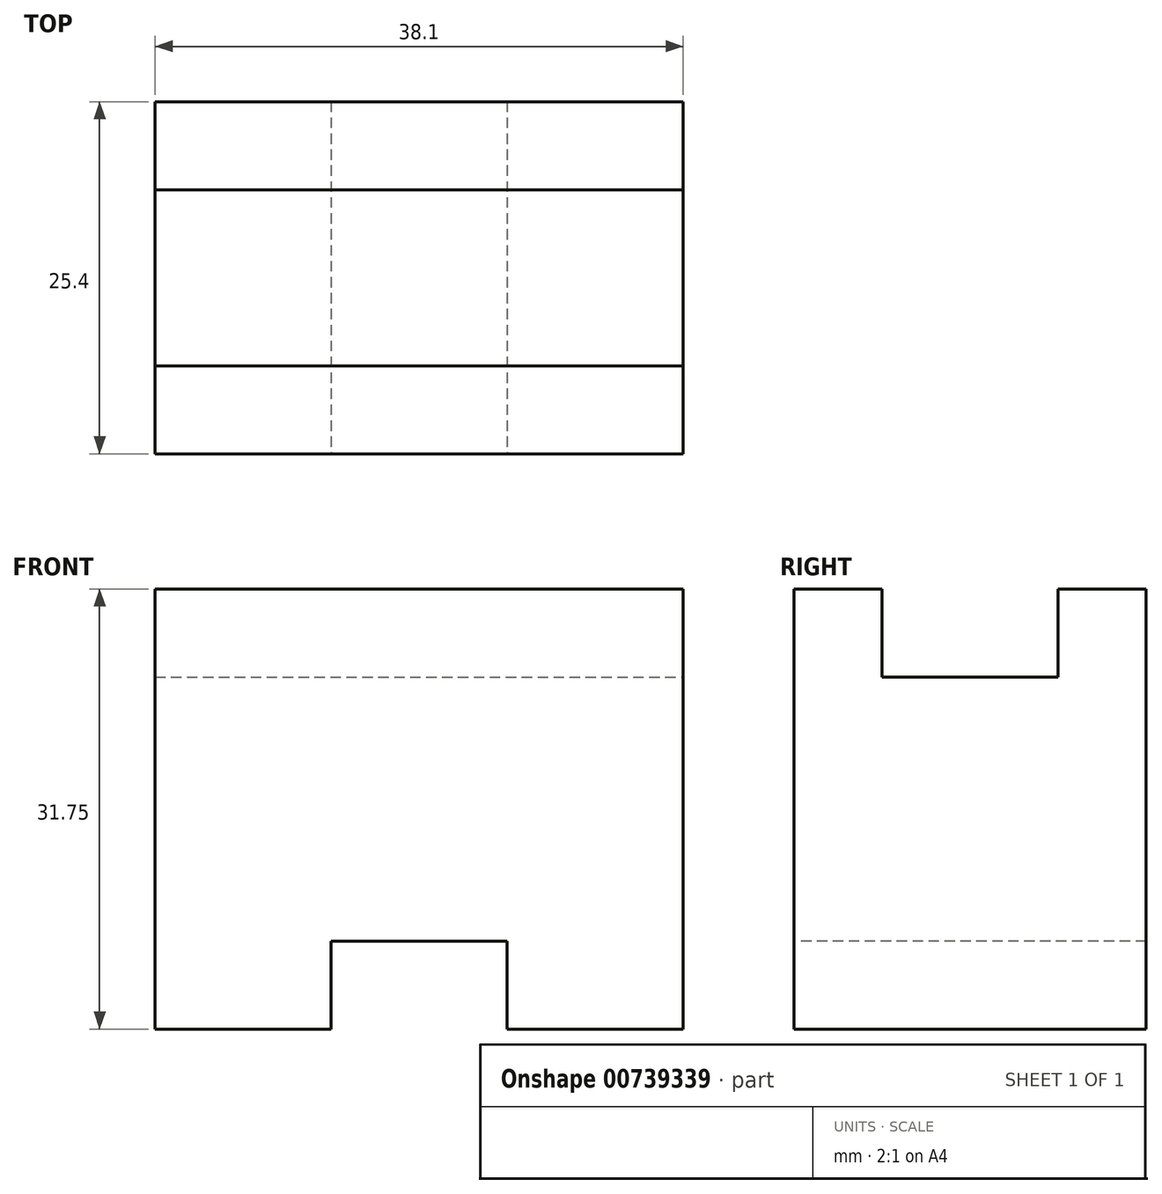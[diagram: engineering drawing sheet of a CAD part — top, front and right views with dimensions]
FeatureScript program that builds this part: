
annotation { "Feature Type Name" : "Feature", "Feature Type Description" : "" }
export const myFeature = defineFeature(function(context is Context, id is Id, definition is map)
    precondition{}
    {
        {
            var Q0;
            Q0=qCreatedBy(makeId("Front.planeOp"),FACE);
            var sketch = newSketch(context, id + "F0", { "sketchPlane" : qUnion([Q0])});
            skLineSegment(sketch, "E0", {"start": v(0, 0) * mm, "end": v(38.1, 0) * mm});
            skLineSegment(sketch, "E1", {"start": v(38.1, 0) * mm, "end": v(38.1, 31.75) * mm});
            skLineSegment(sketch, "E2", {"start": v(38.1, 31.75) * mm, "end": v(0, 31.75) * mm});
            skLineSegment(sketch, "E3", {"start": v(0, 31.75) * mm, "end": v(0, 0) * mm});
            skSolve(sketch);
        }
        {
            var Q0;
            Q0 = qSketchRegion(id + "F0", true);
            extrude(context, id + "F1", {"entities" : qUnion([Q0]), "depth" : 25.4 * mm, "offsetDistance" : 25.4 * mm});
        }
        {
            var Q0;
            Q0=makeQuery(id+"F1.opExtrude","CAP_FACE",FACE,{"disambiguationData":[OSD([sQuery(id+"F0.wireOp",EDGE,"E0"),sQuery(id+"F0.wireOp",EDGE,"E1"),sQuery(id+"F0.wireOp",EDGE,"E2"),sQuery(id+"F0.wireOp",EDGE,"E3")])],"isStart":false});
            var sketch = newSketch(context, id + "F2", { "sketchPlane" : qUnion([Q0])});
            skLineSegment(sketch, "E4.bottom", {"start": v(12.7, 0) * mm, "end": v(25.4, 0) * mm});
            skLineSegment(sketch, "E4.top", {"start": v(12.7, 6.35) * mm, "end": v(25.4, 6.35) * mm});
            skLineSegment(sketch, "E4.left", {"start": v(12.7, 0) * mm, "end": v(12.7, 6.35) * mm});
            skLineSegment(sketch, "E4.right", {"start": v(25.4, 0) * mm, "end": v(25.4, 6.35) * mm});
            skSolve(sketch);
        }
        {
            var Q0;
            Q0 = qSketchRegion(id + "F2", true);
            extrude(context, id + "F3", {"entities" : qUnion([Q0]), "operationType" : NewBodyOperationType.REMOVE, "oppositeDirection" : true, "depth" : 25.4 * mm, "offsetDistance" : 25.4 * mm});
        }
        {
            var Q0;
            Q0=makeQuery(id+"F1.opExtrude","SWEPT_FACE",FACE,{"disambiguationData":[OSD([sQuery(id+"F0.wireOp",EDGE,"E2")])]});
            var sketch = newSketch(context, id + "F4", { "sketchPlane" : qUnion([Q0])});
            skLineSegment(sketch, "E5.bottom", {"start": v(0, -19.05) * mm, "end": v(38.1, -19.05) * mm});
            skLineSegment(sketch, "E5.top", {"start": v(0, -6.35) * mm, "end": v(38.1, -6.35) * mm});
            skLineSegment(sketch, "E5.left", {"start": v(0, -19.05) * mm, "end": v(0, -6.35) * mm});
            skLineSegment(sketch, "E5.right", {"start": v(38.1, -19.05) * mm, "end": v(38.1, -6.35) * mm});
            skSolve(sketch);
        }
        {
            var Q0;
            Q0 = qSketchRegion(id + "F4", true);
            extrude(context, id + "F5", {"entities" : qUnion([Q0]), "operationType" : NewBodyOperationType.REMOVE, "oppositeDirection" : true, "depth" : 6.35 * mm, "offsetDistance" : 25.4 * mm});
        }
    });
